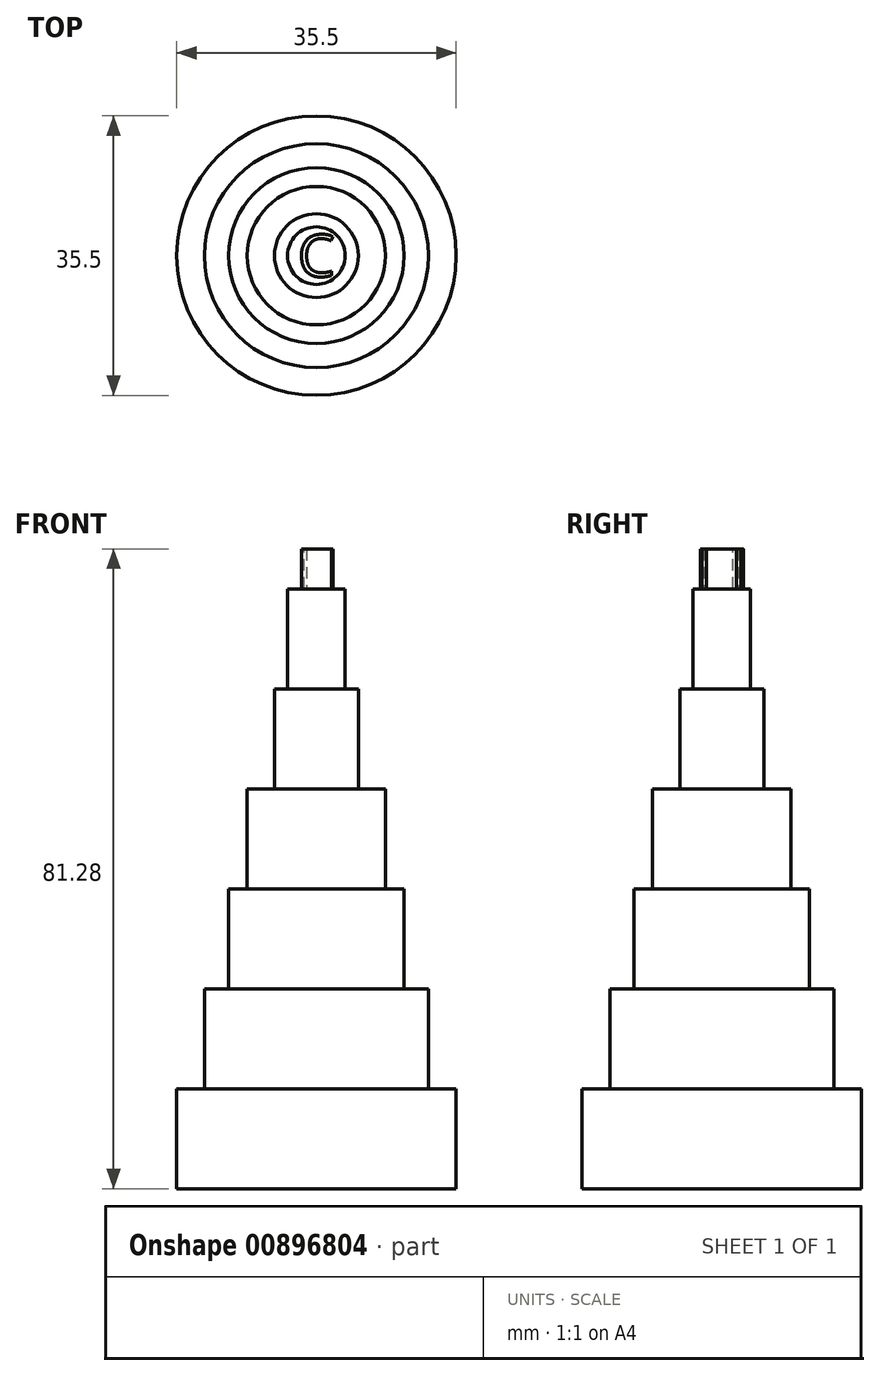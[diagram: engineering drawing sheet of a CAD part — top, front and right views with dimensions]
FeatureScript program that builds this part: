
annotation { "Feature Type Name" : "Feature", "Feature Type Description" : "" }
export const myFeature = defineFeature(function(context is Context, id is Id, definition is map)
    precondition{}
    {
        {
            var Q0;
            Q0=qCreatedBy(makeId("Top.planeOp"),FACE);
            var sketch = newSketch(context, id + "F0", { "sketchPlane" : qUnion([Q0])});
            skCircle(sketch, "E0", {"center": v(0, 0) * mm, "radius": 17.75 * mm});
            skSolve(sketch);
        }
        {
            var Q0;
            Q0 = qSketchRegion(id + "F0", true);
            extrude(context, id + "F1", {"entities" : qUnion([Q0]), "depth" : 12.7 * mm, "offsetDistance" : 25.4 * mm});
        }
        {
            var Q0;
            Q0=qCreatedBy(makeId("Top.planeOp"),FACE);
            var sketch = newSketch(context, id + "F2", { "sketchPlane" : qUnion([Q0])});
            skCircle(sketch, "E1", {"center": v(0, 0) * mm, "radius": 14.22 * mm});
            skSolve(sketch);
        }
        {
            var Q0;
            Q0 = qSketchRegion(id + "F2", true);
            extrude(context, id + "F3", {"entities" : qUnion([Q0]), "operationType" : NewBodyOperationType.ADD, "depth" : 25.4 * mm, "offsetDistance" : 25.4 * mm});
        }
        {
            var Q0;
            Q0=qCreatedBy(makeId("Top.planeOp"),FACE);
            var sketch = newSketch(context, id + "F4", { "sketchPlane" : qUnion([Q0])});
            skCircle(sketch, "E2", {"center": v(0, 0) * mm, "radius": 11.16 * mm});
            skSolve(sketch);
        }
        {
            var Q0;
            Q0 = qSketchRegion(id + "F4", true);
            extrude(context, id + "F5", {"entities" : qUnion([Q0]), "operationType" : NewBodyOperationType.ADD, "depth" : 38.1 * mm, "offsetDistance" : 25.4 * mm});
        }
        {
            var Q0;
            Q0=qCreatedBy(makeId("Top.planeOp"),FACE);
            var sketch = newSketch(context, id + "F6", { "sketchPlane" : qUnion([Q0])});
            skCircle(sketch, "E3", {"center": v(0, 0) * mm, "radius": 8.79 * mm});
            skSolve(sketch);
        }
        {
            var Q0;
            Q0 = qSketchRegion(id + "F6", true);
            extrude(context, id + "F7", {"entities" : qUnion([Q0]), "operationType" : NewBodyOperationType.ADD, "depth" : 50.8 * mm, "offsetDistance" : 25.4 * mm});
        }
        {
            var Q0;
            Q0=qCreatedBy(makeId("Top.planeOp"),FACE);
            var sketch = newSketch(context, id + "F8", { "sketchPlane" : qUnion([Q0])});
            skCircle(sketch, "E4", {"center": v(0, 0) * mm, "radius": 5.33 * mm});
            skSolve(sketch);
        }
        {
            var Q0;
            Q0 = qSketchRegion(id + "F8", true);
            extrude(context, id + "F9", {"entities" : qUnion([Q0]), "operationType" : NewBodyOperationType.ADD, "depth" : 63.5 * mm, "offsetDistance" : 25.4 * mm});
        }
        {
            var Q0;
            Q0=qCreatedBy(makeId("Top.planeOp"),FACE);
            var sketch = newSketch(context, id + "F10", { "sketchPlane" : qUnion([Q0])});
            skCircle(sketch, "E5", {"center": v(0, 0) * mm, "radius": 3.66 * mm});
            skSolve(sketch);
        }
        {
            var Q0;
            Q0 = qSketchRegion(id + "F10", true);
            extrude(context, id + "F11", {"entities" : qUnion([Q0]), "operationType" : NewBodyOperationType.ADD, "depth" : 76.2 * mm, "offsetDistance" : 25.4 * mm});
        }
        {
            var Q0;
            Q0=qCreatedBy(makeId("Top.planeOp"),FACE);
            var sketch = newSketch(context, id + "F12", { "sketchPlane" : qUnion([Q0])});
            skText(sketch, "E6", { "text": "C", "fontName": "OpenSans-Regular.ttf"});
            const initialGuessF12  = {"E6": [-0.00235, -0.00265, 1, 0, 0.00534]};
            skSetInitialGuess(sketch, initialGuessF12);
            skSolve(sketch);
        }
        {
            var Q0;
            Q0 = qSketchRegion(id + "F12", true);
            extrude(context, id + "F13", {"entities" : qUnion([Q0]), "operationType" : NewBodyOperationType.ADD, "depth" : 81.28 * mm, "offsetDistance" : 25.4 * mm});
        }
    });
